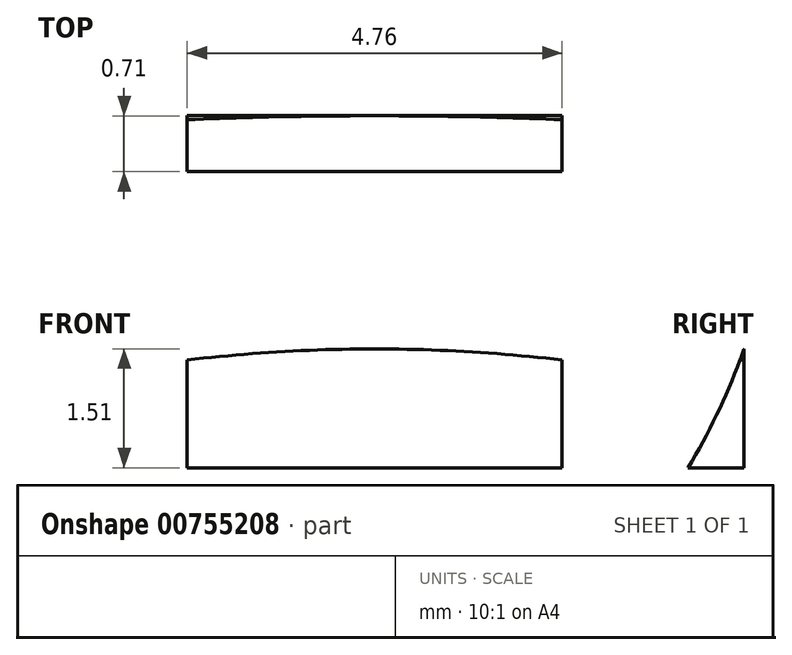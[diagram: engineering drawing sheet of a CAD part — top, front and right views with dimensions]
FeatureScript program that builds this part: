
annotation { "Feature Type Name" : "Feature", "Feature Type Description" : "" }
export const myFeature = defineFeature(function(context is Context, id is Id, definition is map)
    precondition{}
    {
        {
            var Q0;
            Q0=qCreatedBy(makeId("Front.planeOp"),FACE);
            var sketch = newSketch(context, id + "F0", { "sketchPlane" : qUnion([Q0])});
            skArc(sketch, "E0", {"start": v(2.38, 20.08) * mm, "mid": v(0, 20.22) * mm, "end": v(-2.38, 20.08) * mm});
            skArc(sketch, "E1", {"start": v(7.68, 17.22) * mm, "mid": v(0.14, 18.86) * mm, "end": v(-7.42, 17.34) * mm, "construction": true});
            skLineSegment(sketch, "E2", {"start": v(0, 0) * mm, "end": v(0, 13.28) * mm, "construction": true});
            skLineSegment(sketch, "E3", {"start": v(0, 18.7) * mm, "end": v(-2.38, 18.7) * mm});
            skLineSegment(sketch, "E4", {"start": v(-2.38, 18.7) * mm, "end": v(-2.38, 20.08) * mm});
            skLineSegment(sketch, "E5", {"start": v(0, 18.7) * mm, "end": v(2.38, 18.7) * mm});
            skLineSegment(sketch, "E6", {"start": v(2.38, 18.7) * mm, "end": v(2.38, 20.08) * mm});
            skLineSegment(sketch, "E7", {"start": v(0, 18.7) * mm, "end": v(0, 18.7) * mm});
            skSolve(sketch);
        }
        {
            var Q0;
            Q0 = qSketchRegion(id + "F0", true);
            extrude(context, id + "F1", {"entities" : qUnion([Q0]), "oppositeDirection" : true, "depth" : 0.71 * mm, "offsetDistance" : 25.4 * mm});
        }
        {
            var Q0;
            Q0=qCreatedBy(makeId("Right.planeOp"),FACE);
            var sketch = newSketch(context, id + "F2", { "sketchPlane" : qUnion([Q0])});
            skCircle(sketch, "E8", {"center": v(-6.79, 22.83) * mm, "radius": 7.94 * mm});
            skSolve(sketch);
        }
        {
            var Q0;
            Q0 = qSketchRegion(id + "F2", true);
            extrude(context, id + "F3", {"entities" : qUnion([Q0]), "operationType" : NewBodyOperationType.REMOVE, "oppositeDirection" : true, "depth" : 4.76 * mm, "offsetDistance" : 25.4 * mm, "symmetric" : true});
        }
    });
